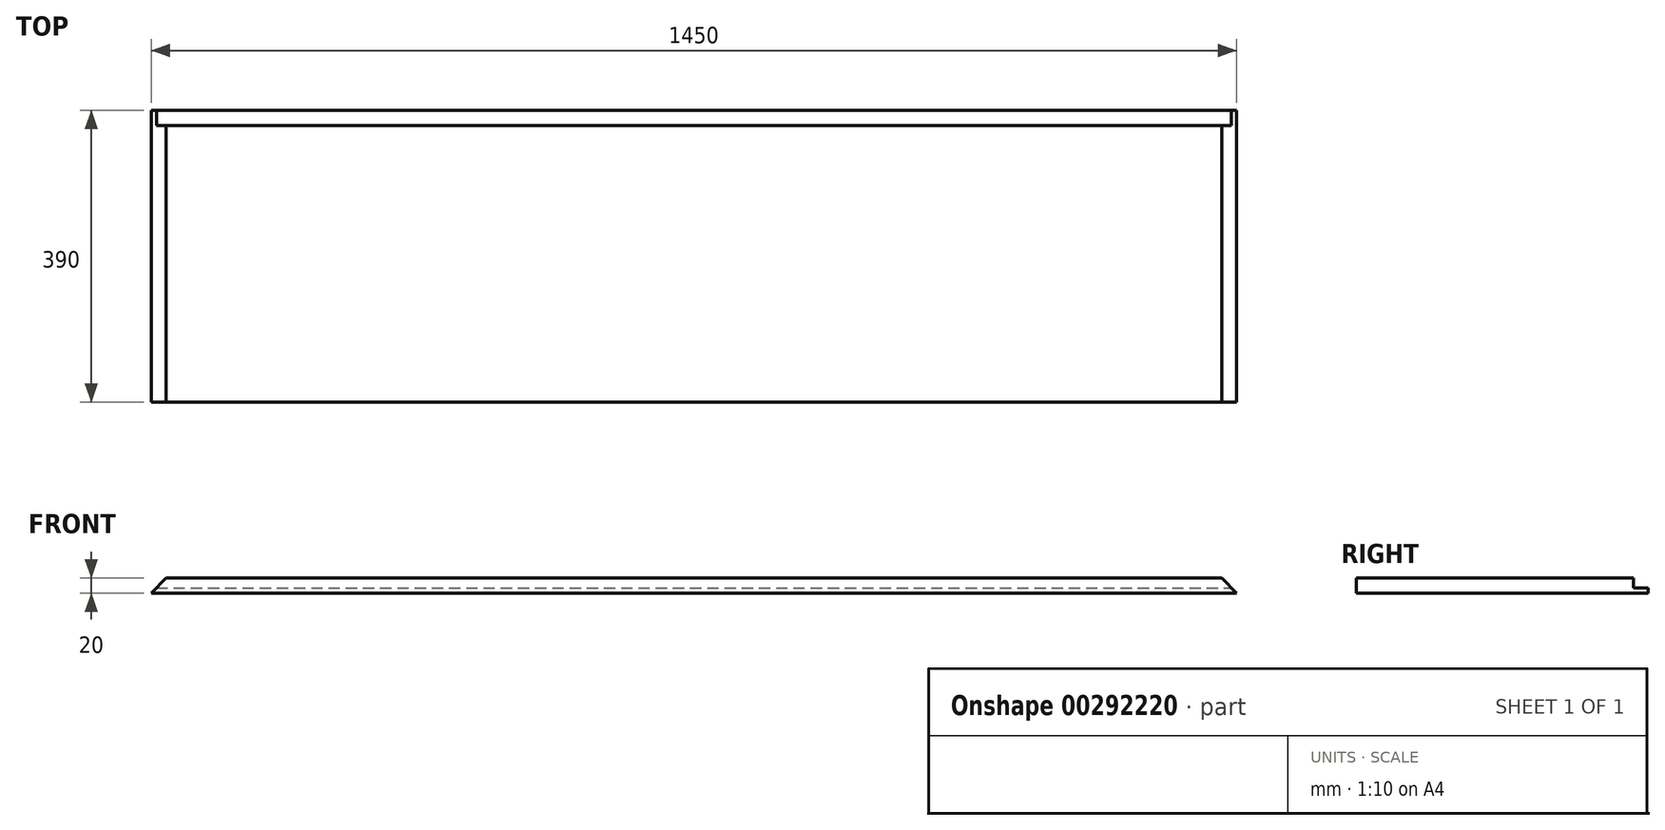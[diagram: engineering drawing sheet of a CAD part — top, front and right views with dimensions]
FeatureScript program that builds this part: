
annotation { "Feature Type Name" : "Feature", "Feature Type Description" : "" }
export const myFeature = defineFeature(function(context is Context, id is Id, definition is map)
    precondition{}
    {
        {
            var Q0;
            Q0=qCreatedBy(makeId("Top.planeOp"),FACE);
            var sketch = newSketch(context, id + "F0", { "sketchPlane" : qUnion([Q0])});
            skPoint(sketch, "E0.middle", {"position": v(0, 0) * mm});
            skLineSegment(sketch, "E1.bottom", {"start": v(725, 207.5) * mm, "end": v(-725, 207.5) * mm});
            skLineSegment(sketch, "E1.top", {"start": v(725, -207.5) * mm, "end": v(-725, -207.5) * mm});
            skLineSegment(sketch, "E1.left", {"start": v(725, 207.5) * mm, "end": v(725, -207.5) * mm});
            skLineSegment(sketch, "E1.right", {"start": v(-725, 207.5) * mm, "end": v(-725, -207.5) * mm});
            skSolve(sketch);
        }
        {
            var Q0;
            Q0=qSketchRegion(id+"F0",true);
            extrude(context, id + "F1", {"entities" : qUnion([Q0]), "depth" : 20 * mm});
        }
        {
            var Q0;
            Q0=makeQuery(id+"F1.opExtrude","SWEPT_FACE",FACE,{"disambiguationData":[OSD([sQuery(id+"F0.wireOp",EDGE,"E1.left")])]});
            var sketch = newSketch(context, id + "F2", { "sketchPlane" : qUnion([Q0])});
            skLineSegment(sketch, "E2.bottom", {"start": v(207.5, 20) * mm, "end": v(187.5, 20) * mm});
            skLineSegment(sketch, "E2.top", {"start": v(207.5, 7) * mm, "end": v(187.5, 7) * mm});
            skLineSegment(sketch, "E2.left", {"start": v(207.5, 20) * mm, "end": v(207.5, 7) * mm});
            skLineSegment(sketch, "E2.right", {"start": v(187.5, 20) * mm, "end": v(187.5, 7) * mm});
            skSolve(sketch);
        }
        {
            var Q0;
            Q0=qSketchRegion(id+"F2",true);
            extrude(context, id + "F3", {"entities" : qUnion([Q0]), "operationType" : NewBodyOperationType.REMOVE, "oppositeDirection" : true, "depth" : 1450 * mm});
        }
        {
            var Q0;
            Q0=makeQuery(id+"F1.opExtrude","SWEPT_FACE",FACE,{"disambiguationData":[OSD([sQuery(id+"F0.wireOp",EDGE,"E1.top")])]});
            var sketch = newSketch(context, id + "F4", { "sketchPlane" : qUnion([Q0])});
            skLineSegment(sketch, "E3", {"start": v(725, 20) * mm, "end": v(725, 0) * mm});
            skLineSegment(sketch, "E4", {"start": v(725, 0) * mm, "end": v(705, 20) * mm});
            skLineSegment(sketch, "E5", {"start": v(705, 20) * mm, "end": v(725, 20) * mm});
            skLineSegment(sketch, "E6", {"start": v(-725, 0) * mm, "end": v(-705, 20) * mm});
            skLineSegment(sketch, "E7", {"start": v(-705, 20) * mm, "end": v(-725, 20) * mm});
            skLineSegment(sketch, "E8", {"start": v(-725, 20) * mm, "end": v(-725, 0) * mm});
            skSolve(sketch);
        }
        {
            var Q0;
            Q0=qSketchRegion(id+"F4",true);
            extrude(context, id + "F5", {"entities" : qUnion([Q0]), "operationType" : NewBodyOperationType.REMOVE, "oppositeDirection" : true, "depth" : 510 * mm});
        }
        {
            var Q0;
            Q0=makeQuery(id+"F1.opExtrude","CAP_FACE",FACE,{"disambiguationData":[OSD([sQuery(id+"F0.wireOp",EDGE,"E1.bottom"),sQuery(id+"F0.wireOp",EDGE,"E1.top"),sQuery(id+"F0.wireOp",EDGE,"E1.left"),sQuery(id+"F0.wireOp",EDGE,"E1.right")])],"isStart":true});
            var sketch = newSketch(context, id + "F6", { "sketchPlane" : qUnion([Q0])});
            skLineSegment(sketch, "E9.bottom", {"start": v(-725, 207.5) * mm, "end": v(725, 207.5) * mm});
            skLineSegment(sketch, "E9.top", {"start": v(-725, 182.5) * mm, "end": v(725, 182.5) * mm});
            skLineSegment(sketch, "E9.left", {"start": v(-725, 207.5) * mm, "end": v(-725, 182.5) * mm});
            skLineSegment(sketch, "E9.right", {"start": v(725, 207.5) * mm, "end": v(725, 182.5) * mm});
            skSolve(sketch);
        }
        {
            var Q0;
            Q0 = qSketchRegion(id + "F6", true);
            extrude(context, id + "F7", {"entities" : qUnion([Q0]), "operationType" : NewBodyOperationType.REMOVE, "oppositeDirection" : true, "depth" : 25 * mm});
        }
    });
